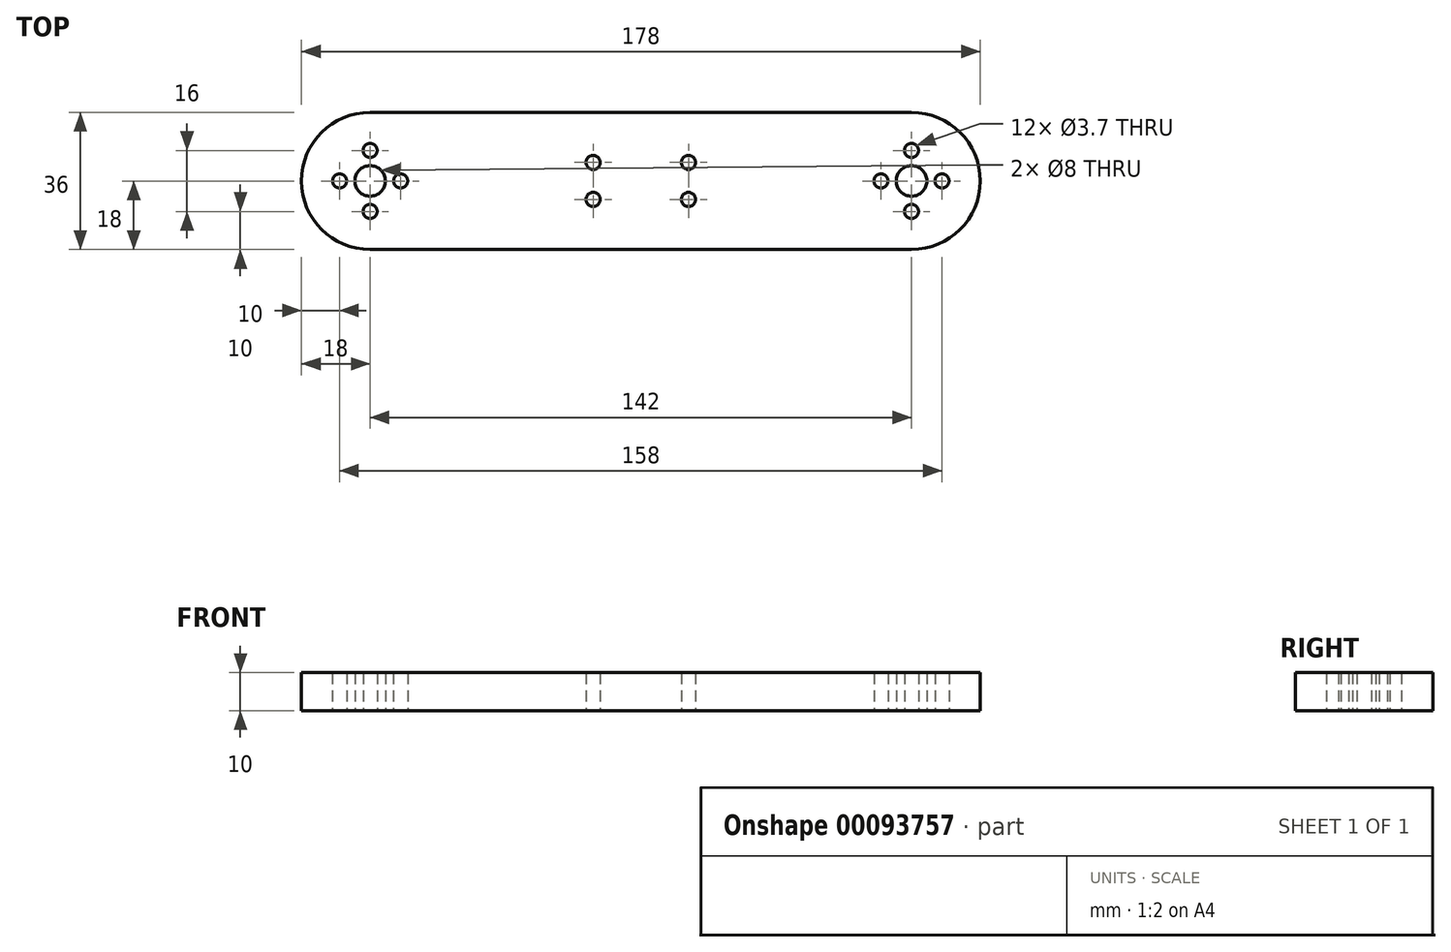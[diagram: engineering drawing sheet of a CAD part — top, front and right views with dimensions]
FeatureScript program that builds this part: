
annotation { "Feature Type Name" : "Feature", "Feature Type Description" : "" }
export const myFeature = defineFeature(function(context is Context, id is Id, definition is map)
    precondition{}
    {
        {
            var Q0;
            Q0=qCreatedBy(makeId("Top.planeOp"),FACE);
            var sketch = newSketch(context, id + "F0", { "sketchPlane" : qUnion([Q0])});
            skArc(sketch, "E0", {"start": v(71, -18) * mm, "mid": v(89, 0) * mm, "end": v(71, 18) * mm});
            skArc(sketch, "E1", {"start": v(-71, 18) * mm, "mid": v(-89, 0) * mm, "end": v(-71, -18) * mm});
            skCircle(sketch, "E2", {"center": v(-71, 0) * mm, "radius": 4 * mm});
            skCircle(sketch, "E3", {"center": v(-71, 8) * mm, "radius": 1.85 * mm});
            skCircle(sketch, "E4", {"center": v(-71, -8) * mm, "radius": 1.85 * mm});
            skCircle(sketch, "E5", {"center": v(-79, 0) * mm, "radius": 1.85 * mm});
            skCircle(sketch, "E6", {"center": v(-63, 0) * mm, "radius": 1.85 * mm});
            skCircle(sketch, "E7", {"center": v(71, 0) * mm, "radius": 4 * mm});
            skCircle(sketch, "E8", {"center": v(71, 8) * mm, "radius": 1.85 * mm});
            skCircle(sketch, "E9", {"center": v(71, -8) * mm, "radius": 1.85 * mm});
            skCircle(sketch, "E10", {"center": v(63, 0) * mm, "radius": 1.85 * mm});
            skCircle(sketch, "E11", {"center": v(79, 0) * mm, "radius": 1.85 * mm});
            skCircle(sketch, "E12", {"center": v(12.5, 4.85) * mm, "radius": 1.85 * mm});
            skCircle(sketch, "E13", {"center": v(12.5, -4.85) * mm, "radius": 1.85 * mm});
            skCircle(sketch, "E14", {"center": v(-12.5, -4.85) * mm, "radius": 1.85 * mm});
            skCircle(sketch, "E15", {"center": v(-12.5, 4.85) * mm, "radius": 1.85 * mm});
            skLineSegment(sketch, "E16", {"start": v(71, 18) * mm, "end": v(-71, 18) * mm});
            skLineSegment(sketch, "E17", {"start": v(71, 9.85) * mm, "end": v(71, 6.15) * mm});
            skLineSegment(sketch, "E18", {"start": v(71, -18) * mm, "end": v(-71, -18) * mm});
            skLineSegment(sketch, "E19", {"start": v(-71, -9.85) * mm, "end": v(-71, -6.15) * mm});
            skLineSegment(sketch, "E20.trimOffspring", {"start": v(-71, 6.15) * mm, "end": v(-71, 9.85) * mm});
            skLineSegment(sketch, "E21.trimOffspring", {"start": v(71, -6.15) * mm, "end": v(71, -9.85) * mm});
            skSolve(sketch);
        }
        {
            var Q0;
            Q0=makeQuery(id+"F0.imprint","IMPRINT",FACE,{"disambiguationData":[TD([[makeQuery(id+"F0.imprint","IMPRINT",EDGE,{"derivedFrom":sQuery(id+"F0.wireOp",EDGE,"E0")}),1.0]])]});
            extrude(context, id + "F1", {"entities" : qUnion([Q0]), "depth" : 10 * mm});
        }
    });
